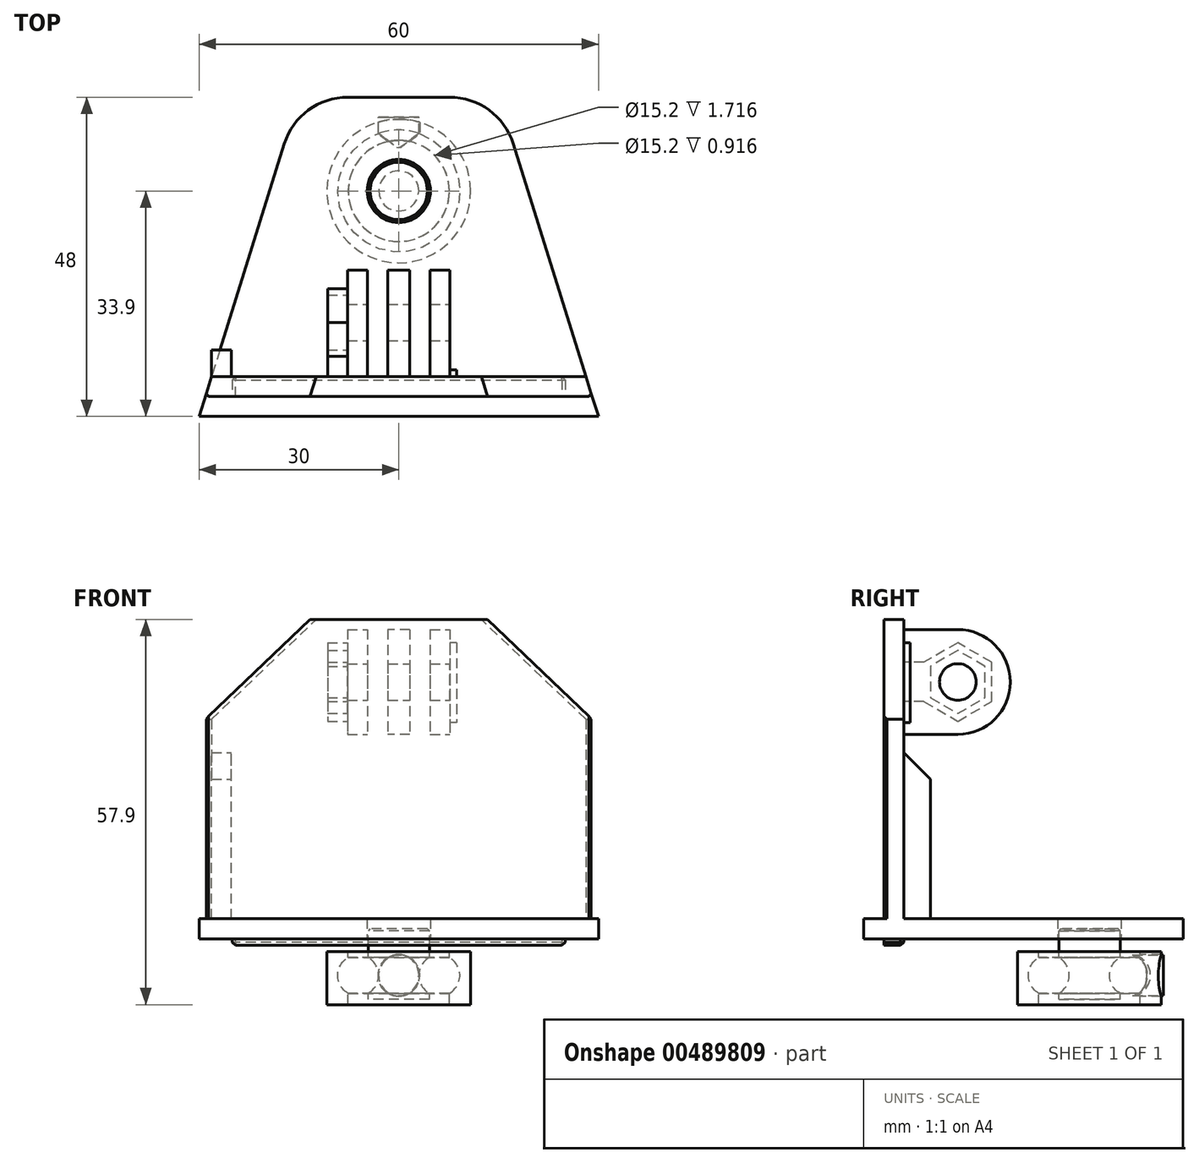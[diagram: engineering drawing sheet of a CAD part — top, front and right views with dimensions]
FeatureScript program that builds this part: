
annotation { "Feature Type Name" : "Feature", "Feature Type Description" : "" }
export const myFeature = defineFeature(function(context is Context, id is Id, definition is map)
    precondition{}
    {
        {
            var Q0;
            Q0=qCreatedBy(makeId("Top.planeOp"),FACE);
            var sketch = newSketch(context, id + "F0", { "sketchPlane" : qUnion([Q0])});
            skArc(sketch, "E0", {"start": v(3, 0) * mm, "mid": v(0, 3) * mm, "end": v(-3, 0) * mm});
            skLineSegment(sketch, "E1", {"start": v(3, 0) * mm, "end": v(-3, 0) * mm});
            skLineSegment(sketch, "E2", {"start": v(0, 0) * mm, "end": v(0, -6.1) * mm, "construction": true});
            skSolve(sketch);
        }
        {
            var Q0;
            Q0=qCreatedBy(makeId("Right.planeOp"),FACE);
            var sketch = newSketch(context, id + "F1", { "sketchPlane" : qUnion([Q0])});
            skCircle(sketch, "E3", {"center": v(0, 0) * mm, "radius": 3.08 * mm});
            skLineSegment(sketch, "E4", {"start": v(0, 0) * mm, "end": v(-12.4, 0) * mm, "construction": true});
            skLineSegment(sketch, "E5", {"start": v(-12.4, 8.14) * mm, "end": v(-12.4, -5.03) * mm, "construction": true});
            skLineSegment(sketch, "E6", {"start": v(0, 0) * mm, "end": v(0, 3.76) * mm, "construction": true});
            skLineSegment(sketch, "E7", {"start": v(-6.1, 3.76) * mm, "end": v(-6.1, -2.41) * mm, "construction": true});
            skSolve(sketch);
        }
        {
            var Q0;
            Q0=sQuery(id+"F1.wireOp",EDGE,"E3");
            var Q1;
            Q1=sQuery(id+"F1.wireOp",EDGE,"E7");
            revolve(context, id + "F2", {"bodyType" : ExtendedToolBodyType.SURFACE, "surfaceEntities" : qUnion([Q0]), "axis" : qUnion([Q1]), "revolveType" : RevolveType.FULL});
        }
        {
            var Q0;
            Q0=qCreatedBy(makeId("Right.planeOp"),FACE);
            var sketch = newSketch(context, id + "F3", { "sketchPlane" : qUnion([Q0])});
            skCircle(sketch, "E8.0", {"center": v(0, 0) * mm, "radius": 3.08 * mm});
            skLineSegment(sketch, "E9.0", {"start": v(-6.1, 3.76) * mm, "end": v(-6.1, -2.41) * mm});
            skLineSegment(sketch, "E9.1", {"start": v(0, 0) * mm, "end": v(-12.4, 0) * mm});
            skPoint(sketch, "E10.rect.middle", {"position": v(-6.1, 0) * mm});
            skLineSegment(sketch, "E11", {"start": v(-1.5, 7) * mm, "end": v(-1.5, -3.6) * mm});
            skLineSegment(sketch, "E12", {"start": v(-1.5, -3.6) * mm, "end": v(-6.1, -3.6) * mm});
            skLineSegment(sketch, "E13", {"start": v(-6.1, -3.6) * mm, "end": v(-6.1, 7) * mm});
            skLineSegment(sketch, "E14", {"start": v(-6.1, 7) * mm, "end": v(-1.5, 7) * mm});
            skLineSegment(sketch, "E15", {"start": v(4.7, 3.6) * mm, "end": v(4.7, -4.4) * mm});
            skLineSegment(sketch, "E16", {"start": v(4.7, -4.4) * mm, "end": v(1.5, -4.4) * mm});
            skLineSegment(sketch, "E17", {"start": v(4.7, 3.6) * mm, "end": v(1.5, 3.6) * mm});
            skLineSegment(sketch, "E18", {"start": v(1.5, 3.6) * mm, "end": v(1.5, -4.4) * mm});
            skSolve(sketch);
        }
        {
            var Q0;
            {var subQ0=sQuery(id+"F3.wireOp",EDGE,"E14");Q0=makeQuery(id+"F3.imprint","IMPRINT",FACE,{"disambiguationData":[TD([[makeQuery(id+"F3.imprint","IMPRINT",EDGE,{"derivedFrom":subQ0}),-1.0]])]});}
            var Q1;
            {var subQ3=sQuery(id+"F3.wireOp",EDGE,"E12");Q1=makeQuery(id+"F3.imprint","IMPRINT",FACE,{"disambiguationData":[TD([[makeQuery(id+"F3.imprint","IMPRINT",EDGE,{"derivedFrom":subQ3}),-1.0]])]});}
            var Q2;
            Q2=sQuery(id+"F3.wireOp",EDGE,"E9.0");
            revolve(context, id + "F4", {"entities" : qUnion([Q0, Q1]), "axis" : qUnion([Q2]), "revolveType" : RevolveType.FULL});
        }
        {
            var Q0;
            Q0=makeQuery(id+"F3.imprint","IMPRINT",FACE,{"disambiguationData":[TD([[makeQuery(id+"F3.imprint","IMPRINT",EDGE,{"derivedFrom":sQuery(id+"F3.wireOp",EDGE,"E15")}),-1.0]])]});
            var Q1;
            Q1=sQuery(id+"F3.wireOp",EDGE,"E9.0");
            revolve(context, id + "F5", {"entities" : qUnion([Q0]), "axis" : qUnion([Q1]), "revolveType" : RevolveType.FULL});
        }
        {
            var Q0;
            Q0=qCreatedBy(makeId("Front.planeOp"),FACE);
            var sketch = newSketch(context, id + "F6", { "sketchPlane" : qUnion([Q0])});
            skCircle(sketch, "E19", {"center": v(0, 0) * mm, "radius": 3.15 * mm});
            skSolve(sketch);
        }
        {
            var Q0;
            Q0=makeQuery(id+"F6.imprint","IMPRINT",FACE,{"disambiguationData":[TD([[makeQuery(id+"F6.imprint","IMPRINT",EDGE,{"derivedFrom":sQuery(id+"F6.wireOp",EDGE,"E19")}),1.0]])]});
            var Q1;
            Q1=makeQuery(id+"F5.opRevolve","SWEPT_FACE",FACE,{"disambiguationData":[OSD([sQuery(id+"F3.wireOp",EDGE,"E15")])]});
            extrude(context, id + "F7", {"entities" : qUnion([Q0]), "operationType" : NewBodyOperationType.REMOVE, "endBound" : BoundingType.UP_TO_SURFACE, "oppositeDirection" : true, "endBoundEntityFace" : qUnion([Q1]), "depth" : 25 * mm});
        }
        {
            var Q0;
            Q0=qCreatedBy(makeId("Front.planeOp"),FACE);
            var sketch = newSketch(context, id + "F8", { "sketchPlane" : qUnion([Q0])});
            skLineSegment(sketch, "E20.rect.bottom", {"start": v(13.05, 1.97) * mm, "end": v(8.99, 1.97) * mm});
            skLineSegment(sketch, "E20.rect.top", {"start": v(13.05, 8.89) * mm, "end": v(8.99, 8.89) * mm});
            skLineSegment(sketch, "E20.rect.left", {"start": v(13.05, 1.97) * mm, "end": v(13.05, 8.89) * mm});
            skLineSegment(sketch, "E20.rect.right", {"start": v(8.99, 1.97) * mm, "end": v(8.99, 8.89) * mm});
            skPoint(sketch, "E20.rect.middle", {"position": v(11.02, 5.43) * mm});
            skSolve(sketch);
        }
        {
            var Q0;
            Q0=makeQuery(id+"F8.imprint","IMPRINT",FACE,{"disambiguationData":[TD([[makeQuery(id+"F8.imprint","IMPRINT",EDGE,{"derivedFrom":sQuery(id+"F8.wireOp",EDGE,"E20.rect.bottom")}),-1.0]])]});
            cPlane(context, id + "F9", {"entities" : qUnion([Q0]), "cplaneType" : CPlaneType.OFFSET, "offset" : 5 * mm, "oppositeDirection" : true, "width" : 150 * mm, "height" : 150 * mm});
        }
        {
            var Q0;
            Q0=qCreatedBy(id+"F9.planeOp",FACE);
            var sketch = newSketch(context, id + "F10", { "sketchPlane" : qUnion([Q0])});
            skCircle(sketch, "E21", {"center": v(0, 0) * mm, "radius": 3.05 * mm});
            skSolve(sketch);
        }
        {
            var Q0;
            Q0=makeQuery(id+"F10.imprint","IMPRINT",FACE,{"disambiguationData":[TD([[makeQuery(id+"F10.imprint","IMPRINT",EDGE,{"derivedFrom":sQuery(id+"F10.wireOp",EDGE,"E21")}),1.0]])]});
            var Q1;
            Q1=makeQuery(id+"F5.opRevolve","SWEPT_FACE",FACE,{"disambiguationData":[OSD([sQuery(id+"F3.wireOp",EDGE,"E8.0")])]});
            extrude(context, id + "F11", {"entities" : qUnion([Q0]), "endBound" : BoundingType.UP_TO_SURFACE, "endBoundEntityFace" : qUnion([Q1]), "depth" : 25 * mm});
        }
        {
            var Q0;
            Q0=makeQuery(id+"F4.opRevolve","SWEPT_EDGE",EDGE,{"disambiguationData":[OSD([sQuery(id+"F3.wireOp",EDGE,"E11"),sQuery(id+"F3.wireOp",EDGE,"E14")])]});
            chamfer(context, id + "F12", {"entities" : qUnion([Q0]), "width" : 0.3 * mm, "tangentPropagation" : true});
        }
        {
            var Q0;
            Q0=makeQuery(id+"F4.opRevolve","SWEPT_FACE",FACE,{"disambiguationData":[OSD([sQuery(id+"F3.wireOp",EDGE,"E14")])]});
            var sketch = newSketch(context, id + "F13", { "sketchPlane" : qUnion([Q0])});
            skLineSegment(sketch, "E22.bottom", {"start": v(-25, -34) * mm, "end": v(25, -34) * mm});
            skLineSegment(sketch, "E22.top", {"start": v(-25, -37) * mm, "end": v(25, -37) * mm});
            skLineSegment(sketch, "E22.left", {"start": v(-25, -34) * mm, "end": v(-25, -37) * mm});
            skLineSegment(sketch, "E22.right", {"start": v(25, -34) * mm, "end": v(25, -37) * mm});
            skLineSegment(sketch, "E23", {"start": v(-30, -40) * mm, "end": v(30, -40) * mm});
            skLineSegment(sketch, "E24", {"start": v(-15, 8) * mm, "end": v(15, 8) * mm});
            skLineSegment(sketch, "E25", {"start": v(-15, 8) * mm, "end": v(-30, -40) * mm});
            skLineSegment(sketch, "E26", {"start": v(15, 8) * mm, "end": v(30, -40) * mm});
            skCircle(sketch, "E27.0", {"center": v(0, -6.1) * mm, "radius": 4.75 * mm});
            skSolve(sketch);
        }
        {
            var Q0;
            Q0=makeQuery(id+"F13.imprint","IMPRINT",FACE,{"disambiguationData":[TD([[makeQuery(id+"F13.imprint","IMPRINT",EDGE,{"derivedFrom":sQuery(id+"F13.wireOp",EDGE,"E22.bottom")}),1.0]])]});
            extrude(context, id + "F14", {"entities" : qUnion([Q0]), "depth" : 3 * mm, "symmetric" : true});
        }
        {
            var Q0;
            Q0=makeQuery(id+"F14.opExtrude","SWEPT_EDGE",EDGE,{"disambiguationData":[OSD([sQuery(id+"F13.wireOp",EDGE,"E24"),sQuery(id+"F13.wireOp",EDGE,"E25")])]});
            var Q1;
            Q1=makeQuery(id+"F14.opExtrude","SWEPT_EDGE",EDGE,{"disambiguationData":[OSD([sQuery(id+"F13.wireOp",EDGE,"E24"),sQuery(id+"F13.wireOp",EDGE,"E26")])]});
            fillet(context, id + "F15", {"entities" : qUnion([Q0, Q1]), "radius" : 10 * mm, "tangentPropagation" : true, "allowEdgeOverflow" : false});
        }
        {
            var Q0;
            Q0=makeQuery(id+"F14.opExtrude","CAP_FACE",FACE,{"disambiguationData":[OSD([sQuery(id+"F13.wireOp",EDGE,"E22.bottom"),sQuery(id+"F13.wireOp",EDGE,"E22.top"),sQuery(id+"F13.wireOp",EDGE,"E22.left"),sQuery(id+"F13.wireOp",EDGE,"E22.right"),sQuery(id+"F13.wireOp",EDGE,"E23"),sQuery(id+"F13.wireOp",EDGE,"E24"),sQuery(id+"F13.wireOp",EDGE,"E25"),sQuery(id+"F13.wireOp",EDGE,"E26"),sQuery(id+"F13.wireOp",EDGE,"E27.0")])],"isStart":false});
            var sketch = newSketch(context, id + "F16", { "sketchPlane" : qUnion([Q0])});
            skLineSegment(sketch, "E28.0", {"start": v(-25, -37) * mm, "end": v(25, -37) * mm});
            skLineSegment(sketch, "E28.1", {"start": v(-25, -34) * mm, "end": v(-25, -37) * mm});
            skLineSegment(sketch, "E28.2", {"start": v(-25, -34) * mm, "end": v(25, -34) * mm});
            skLineSegment(sketch, "E28.3", {"start": v(25, -34) * mm, "end": v(25, -37) * mm});
            skLineSegment(sketch, "E29", {"start": v(-25, -34) * mm, "end": v(-28.12, -34) * mm});
            skLineSegment(sketch, "E30", {"start": v(-28.12, -34) * mm, "end": v(-29.06, -37) * mm});
            skLineSegment(sketch, "E31", {"start": v(-29.06, -37) * mm, "end": v(-25, -37) * mm});
            skLineSegment(sketch, "E32", {"start": v(25, -34) * mm, "end": v(28.12, -34) * mm});
            skLineSegment(sketch, "E33", {"start": v(28.12, -34) * mm, "end": v(29.06, -37) * mm});
            skLineSegment(sketch, "E34", {"start": v(29.06, -37) * mm, "end": v(25, -37) * mm});
            skSolve(sketch);
        }
        {
            var Q0;
            Q0=makeQuery(id+"F16.imprint","IMPRINT",FACE,{"disambiguationData":[TD([[makeQuery(id+"F16.imprint","IMPRINT",EDGE,{"derivedFrom":sQuery(id+"F16.wireOp",EDGE,"E28.3")}),1.0]])]});
            var Q1;
            Q1=makeQuery(id+"F16.imprint","IMPRINT",FACE,{"disambiguationData":[TD([[makeQuery(id+"F16.imprint","IMPRINT",EDGE,{"derivedFrom":sQuery(id+"F16.wireOp",EDGE,"E28.1")}),-1.0]])]});
            var Q2;
            Q2=makeQuery(id+"F16.imprint","IMPRINT",FACE,{"disambiguationData":[TD([[makeQuery(id+"F16.imprint","IMPRINT",EDGE,{"derivedFrom":sQuery(id+"F16.wireOp",EDGE,"E28.0")}),1.0]])]});
            extrude(context, id + "F17", {"entities" : qUnion([Q0, Q1, Q2]), "depth" : 45 * mm});
        }
        {
            var Q0;
            Q0=makeQuery(id+"F16.imprint","IMPRINT",FACE,{"disambiguationData":[TD([[makeQuery(id+"F16.imprint","IMPRINT",EDGE,{"derivedFrom":sQuery(id+"F16.wireOp",EDGE,"E28.0")}),1.0]])]});
            var Q1;
            Q1=makeQuery(id+"F14.opExtrude","CAP_FACE",FACE,{"disambiguationData":[OSD([sQuery(id+"F13.wireOp",EDGE,"E22.bottom"),sQuery(id+"F13.wireOp",EDGE,"E22.top"),sQuery(id+"F13.wireOp",EDGE,"E22.left"),sQuery(id+"F13.wireOp",EDGE,"E22.right"),sQuery(id+"F13.wireOp",EDGE,"E23"),sQuery(id+"F13.wireOp",EDGE,"E24"),sQuery(id+"F13.wireOp",EDGE,"E25"),sQuery(id+"F13.wireOp",EDGE,"E26"),sQuery(id+"F13.wireOp",EDGE,"E27.0")])],"isStart":true});
            extrude(context, id + "F18", {"entities" : qUnion([Q0]), "operationType" : NewBodyOperationType.ADD, "oppositeDirection" : true, "endBoundEntity" : qUnion([Q1]), "depth" : 4 * mm});
        }
        {
            var Q0;
            Q0=makeQuery(id+"F18.opExtrude","SWEPT_EDGE",EDGE,{"disambiguationData":[OSD([sQuery(id+"F16.wireOp",EDGE,"E28.2"),sQuery(id+"F16.wireOp",EDGE,"E28.3"),sQuery(id+"F16.wireOp",EDGE,"E32")])]});
            var Q1;
            Q1=makeQuery(id+"F18.opExtrude","SWEPT_EDGE",EDGE,{"disambiguationData":[OSD([sQuery(id+"F16.wireOp",EDGE,"E28.1"),sQuery(id+"F16.wireOp",EDGE,"E28.2"),sQuery(id+"F16.wireOp",EDGE,"E29")])]});
            var Q2;
            Q2=makeQuery(id+"F18.opExtrude","CAP_EDGE",EDGE,{"disambiguationData":[OSD([sQuery(id+"F16.wireOp",EDGE,"E28.2")])],"isStart":false});
            var Q3;
            Q3=makeQuery(id+"F18.opExtrude","CAP_EDGE",EDGE,{"disambiguationData":[OSD([sQuery(id+"F16.wireOp",EDGE,"E28.3")])],"isStart":false});
            var Q4;
            Q4=makeQuery(id+"F18.opExtrude","CAP_EDGE",EDGE,{"disambiguationData":[OSD([sQuery(id+"F16.wireOp",EDGE,"E28.1")])],"isStart":false});
            chamfer(context, id + "F19", {"entities" : qUnion([Q0, Q1, Q2, Q3, Q4]), "width" : 0.5 * mm, "tangentPropagation" : true});
        }
        {
            var Q0;
            Q0=makeQuery(id+"F17.opExtrude","SWEPT_EDGE",EDGE,{"disambiguationData":[OSD([sQuery(id+"F13.wireOp",EDGE,"E26"),sQuery(id+"F16.wireOp",EDGE,"E33"),sQuery(id+"F16.wireOp",EDGE,"E34")])]});
            var Q1;
            Q1=makeQuery(id+"F17.opExtrude","SWEPT_EDGE",EDGE,{"disambiguationData":[OSD([sQuery(id+"F13.wireOp",EDGE,"E25"),sQuery(id+"F16.wireOp",EDGE,"E30"),sQuery(id+"F16.wireOp",EDGE,"E31")])]});
            chamfer(context, id + "F20", {"entities" : qUnion([Q0, Q1]), "width" : 0.5 * mm, "tangentPropagation" : true});
        }
        {
            var Q0;
            {var subQ0=sQuery(id+"F16.wireOp",EDGE,"E28.2");Q0=makeQuery(id+"F18.boolean.opBoolean","MERGE",FACE,{"derivedFrom":[makeQuery(id+"F17.opExtrude","SWEPT_FACE",FACE,{"disambiguationData":[OSD([subQ0,sQuery(id+"F16.wireOp",EDGE,"E29"),sQuery(id+"F16.wireOp",EDGE,"E32")])]}),makeQuery(id+"F18.opExtrude","SWEPT_FACE",FACE,{"disambiguationData":[OSD([subQ0])]})]});}
            var sketch = newSketch(context, id + "F21", { "sketchPlane" : qUnion([Q0])});
            skLineSegment(sketch, "E35.rect.bottom", {"start": v(-1.65, 51.98) * mm, "end": v(1.65, 51.98) * mm});
            skLineSegment(sketch, "E35.rect.top", {"start": v(-1.65, 36.23) * mm, "end": v(1.65, 36.23) * mm});
            skLineSegment(sketch, "E35.rect.left", {"start": v(-1.65, 51.98) * mm, "end": v(-1.65, 36.23) * mm});
            skLineSegment(sketch, "E35.rect.right", {"start": v(1.65, 51.98) * mm, "end": v(1.65, 36.23) * mm});
            skPoint(sketch, "E35.rect.middle", {"position": v(0, 44.1) * mm});
            skLineSegment(sketch, "E36.bottom", {"start": v(-4.7, 51.98) * mm, "end": v(-7.7, 51.98) * mm});
            skLineSegment(sketch, "E36.top", {"start": v(-4.7, 36.23) * mm, "end": v(-7.7, 36.23) * mm});
            skLineSegment(sketch, "E36.left", {"start": v(-4.7, 51.98) * mm, "end": v(-4.7, 36.23) * mm});
            skLineSegment(sketch, "E36.right", {"start": v(-7.7, 51.98) * mm, "end": v(-7.7, 36.23) * mm});
            skLineSegment(sketch, "E37.bottom", {"start": v(7.7, 51.98) * mm, "end": v(4.7, 51.98) * mm});
            skLineSegment(sketch, "E37.top", {"start": v(7.7, 36.23) * mm, "end": v(4.7, 36.23) * mm});
            skLineSegment(sketch, "E37.left", {"start": v(7.7, 51.98) * mm, "end": v(7.7, 36.23) * mm});
            skLineSegment(sketch, "E37.right", {"start": v(4.7, 51.98) * mm, "end": v(4.7, 36.23) * mm});
            skSolve(sketch);
        }
        {
            var Q0;
            Q0=makeQuery(id+"F21.imprint","IMPRINT",FACE,{"disambiguationData":[TD([[makeQuery(id+"F21.imprint","IMPRINT",EDGE,{"derivedFrom":sQuery(id+"F21.wireOp",EDGE,"E36.bottom")}),1.0]])]});
            var Q1;
            Q1=makeQuery(id+"F21.imprint","IMPRINT",FACE,{"disambiguationData":[TD([[makeQuery(id+"F21.imprint","IMPRINT",EDGE,{"derivedFrom":sQuery(id+"F21.wireOp",EDGE,"E35.rect.bottom")}),-1.0]])]});
            var Q2;
            Q2=makeQuery(id+"F21.imprint","IMPRINT",FACE,{"disambiguationData":[TD([[makeQuery(id+"F21.imprint","IMPRINT",EDGE,{"derivedFrom":sQuery(id+"F21.wireOp",EDGE,"E37.bottom")}),1.0]])]});
            extrude(context, id + "F22", {"entities" : qUnion([Q0, Q1, Q2]), "operationType" : NewBodyOperationType.ADD, "depth" : 16 * mm});
        }
        {
            var Q0;
            {var subQ0=sQuery(id+"F16.wireOp",EDGE,"E28.2");Q0=makeQuery(id+"F18.boolean.opBoolean","MERGE",FACE,{"derivedFrom":[makeQuery(id+"F17.opExtrude","SWEPT_FACE",FACE,{"disambiguationData":[OSD([subQ0,sQuery(id+"F16.wireOp",EDGE,"E29"),sQuery(id+"F16.wireOp",EDGE,"E32")])]}),makeQuery(id+"F18.opExtrude","SWEPT_FACE",FACE,{"disambiguationData":[OSD([subQ0])]})]});}
            var sketch = newSketch(context, id + "F23", { "sketchPlane" : qUnion([Q0])});
            skLineSegment(sketch, "E38.bottom", {"start": v(-28.12, 8.5) * mm, "end": v(-25.12, 8.5) * mm});
            skLineSegment(sketch, "E38.top", {"start": v(-28.13, 33.5) * mm, "end": v(-25.12, 33.5) * mm});
            skLineSegment(sketch, "E38.left", {"start": v(-28.12, 8.5) * mm, "end": v(-28.13, 33.5) * mm});
            skLineSegment(sketch, "E38.right", {"start": v(-25.12, 8.5) * mm, "end": v(-25.12, 33.5) * mm});
            skLineSegment(sketch, "E39.bottom", {"start": v(28.12, 8.5) * mm, "end": v(25.12, 8.5) * mm});
            skLineSegment(sketch, "E39.top", {"start": v(28.12, 33.5) * mm, "end": v(25.12, 33.5) * mm});
            skLineSegment(sketch, "E39.left", {"start": v(28.12, 8.5) * mm, "end": v(28.12, 33.5) * mm});
            skLineSegment(sketch, "E39.right", {"start": v(25.12, 8.5) * mm, "end": v(25.12, 33.5) * mm});
            skSolve(sketch);
        }
        {
            var Q0;
            {Q0=qUnion([makeQuery(id+"F23.imprint","IMPRINT",FACE,{"disambiguationData":[TD([[makeQuery(id+"F23.imprint","IMPRINT",EDGE,{"derivedFrom":sQuery(id+"F23.wireOp",EDGE,"E38.bottom")}),-1.0]])]}),makeQuery(id+"F23.imprint","IMPRINT",FACE,{"disambiguationData":[TD([[makeQuery(id+"F23.imprint","IMPRINT",EDGE,{"derivedFrom":sQuery(id+"F23.wireOp",EDGE,"E39.bottom")}),-1.0]])]})]);}
            extrude(context, id + "F24", {"entities" : qUnion([Q0]), "operationType" : NewBodyOperationType.ADD, "depth" : 4 * mm});
        }
        {
            var Q0;
            Q0=makeQuery(id+"F24.opExtrude","CAP_EDGE",EDGE,{"disambiguationData":[OSD([sQuery(id+"F23.wireOp",EDGE,"E38.top")])],"isStart":false});
            var Q1;
            Q1=makeQuery(id+"F24.opExtrude","CAP_EDGE",EDGE,{"disambiguationData":[OSD([sQuery(id+"F23.wireOp",EDGE,"E39.top")])],"isStart":false});
            chamfer(context, id + "F25", {"entities" : qUnion([Q0, Q1]), "width" : 4 * mm, "tangentPropagation" : true});
        }
        {
            var Q0;
            Q0=makeQuery(id+"F22.opExtrude","SWEPT_FACE",FACE,{"disambiguationData":[OSD([sQuery(id+"F21.wireOp",EDGE,"E36.right")])]});
            var sketch = newSketch(context, id + "F26", { "sketchPlane" : qUnion([Q0])});
            skCircle(sketch, "E40", {"center": v(-25.88, 44.1) * mm, "radius": 2.75 * mm});
            skSolve(sketch);
        }
        {
            var Q0;
            Q0=makeQuery(id+"F26.imprint","IMPRINT",FACE,{"disambiguationData":[TD([[makeQuery(id+"F26.imprint","IMPRINT",EDGE,{"derivedFrom":sQuery(id+"F26.wireOp",EDGE,"E40")}),1.0]])]});
            extrude(context, id + "F27", {"entities" : qUnion([Q0]), "operationType" : NewBodyOperationType.REMOVE, "oppositeDirection" : true, "depth" : 25 * mm});
        }
        {
            var Q0;
            Q0=makeQuery(id+"F22.opExtrude","CAP_EDGE",EDGE,{"disambiguationData":[OSD([sQuery(id+"F21.wireOp",EDGE,"E36.bottom")])],"isStart":false});
            var Q1;
            Q1=makeQuery(id+"F22.opExtrude","CAP_EDGE",EDGE,{"disambiguationData":[OSD([sQuery(id+"F21.wireOp",EDGE,"E35.rect.bottom")])],"isStart":false});
            var Q2;
            Q2=makeQuery(id+"F22.opExtrude","CAP_EDGE",EDGE,{"disambiguationData":[OSD([sQuery(id+"F21.wireOp",EDGE,"E37.bottom")])],"isStart":false});
            var Q3;
            Q3=makeQuery(id+"F22.opExtrude","CAP_EDGE",EDGE,{"disambiguationData":[OSD([sQuery(id+"F21.wireOp",EDGE,"E37.top")])],"isStart":false});
            var Q4;
            Q4=makeQuery(id+"F22.opExtrude","CAP_EDGE",EDGE,{"disambiguationData":[OSD([sQuery(id+"F21.wireOp",EDGE,"E35.rect.top")])],"isStart":false});
            var Q5;
            Q5=makeQuery(id+"F22.opExtrude","CAP_EDGE",EDGE,{"disambiguationData":[OSD([sQuery(id+"F21.wireOp",EDGE,"E36.top")])],"isStart":false});
            fillet(context, id + "F28", {"entities" : qUnion([Q0, Q1, Q2, Q3, Q4, Q5]), "radius" : 7.88 * mm, "tangentPropagation" : true, "allowEdgeOverflow" : false});
        }
        {
            var Q0;
            Q0=makeQuery(id+"F17.opExtrude","CAP_EDGE",EDGE,{"disambiguationData":[OSD([sQuery(id+"F16.wireOp",EDGE,"E30")])],"isStart":false});
            var Q1;
            Q1=makeQuery(id+"F17.opExtrude","CAP_EDGE",EDGE,{"disambiguationData":[OSD([sQuery(id+"F16.wireOp",EDGE,"E33")])],"isStart":false});
            chamfer(context, id + "F29", {"entities" : qUnion([Q0, Q1]), "width" : 15 * mm, "tangentPropagation" : true});
        }
        {
            var Q0;
            Q0=makeQuery(id+"F22.opExtrude","SWEPT_FACE",FACE,{"disambiguationData":[OSD([sQuery(id+"F21.wireOp",EDGE,"E37.left")])]});
            var sketch = newSketch(context, id + "F30", { "sketchPlane" : qUnion([Q0])});
            skCircle(sketch, "E41.0", {"center": v(25.88, 44.1) * mm, "radius": 2.75 * mm});
            skCircle(sketch, "E42.cCircle", {"center": v(25.88, 44.1) * mm, "radius": 4.1 * mm, "construction": true});
            skLineSegment(sketch, "E42.0", {"start": v(29.98, 46.47) * mm, "end": v(29.98, 41.73) * mm});
            skLineSegment(sketch, "E42.1", {"start": v(29.97, 41.73) * mm, "end": v(25.88, 39.37) * mm});
            skLineSegment(sketch, "E42.2", {"start": v(25.88, 39.37) * mm, "end": v(21.78, 41.73) * mm});
            skLineSegment(sketch, "E42.3", {"start": v(21.78, 41.73) * mm, "end": v(21.78, 46.47) * mm});
            skLineSegment(sketch, "E42.4", {"start": v(21.78, 46.47) * mm, "end": v(25.88, 48.83) * mm});
            skLineSegment(sketch, "E42.5", {"start": v(25.88, 48.83) * mm, "end": v(29.98, 46.47) * mm});
            skPoint(sketch, "E42.0.midPoint", {"position": v(29.98, 44.1) * mm});
            skLineSegment(sketch, "E43.0", {"start": v(20.78, 47.04) * mm, "end": v(25.88, 49.99) * mm});
            skLineSegment(sketch, "E43.1", {"start": v(20.78, 41.16) * mm, "end": v(20.78, 47.04) * mm});
            skLineSegment(sketch, "E43.2", {"start": v(25.88, 38.21) * mm, "end": v(20.78, 41.16) * mm});
            skLineSegment(sketch, "E43.3", {"start": v(30.98, 41.16) * mm, "end": v(25.88, 38.21) * mm});
            skLineSegment(sketch, "E43.4", {"start": v(30.97, 47.04) * mm, "end": v(30.97, 41.16) * mm});
            skLineSegment(sketch, "E43.5", {"start": v(25.88, 49.99) * mm, "end": v(30.97, 47.04) * mm});
            skLineSegment(sketch, "E44.bottom", {"start": v(30.98, 41.16) * mm, "end": v(34, 41.16) * mm});
            skLineSegment(sketch, "E44.top", {"start": v(30.98, 47.04) * mm, "end": v(34, 47.04) * mm});
            skLineSegment(sketch, "E44.left", {"start": v(30.98, 41.16) * mm, "end": v(30.98, 47.04) * mm});
            skLineSegment(sketch, "E44.right", {"start": v(34, 41.16) * mm, "end": v(34, 47.04) * mm});
            skSolve(sketch);
        }
        {
            var Q0;
            Q0=makeQuery(id+"F30.imprint","IMPRINT",FACE,{"disambiguationData":[TD([[makeQuery(id+"F30.imprint","IMPRINT",EDGE,{"derivedFrom":sQuery(id+"F30.wireOp",EDGE,"E42.0")}),1.0]])]});
            var Q1;
            Q1=makeQuery(id+"F30.imprint","IMPRINT",FACE,{"disambiguationData":[TD([[makeQuery(id+"F30.imprint","IMPRINT",EDGE,{"derivedFrom":sQuery(id+"F30.wireOp",EDGE,"E44.bottom")}),1.0]])]});
            extrude(context, id + "F31", {"entities" : qUnion([Q0, Q1]), "operationType" : NewBodyOperationType.ADD, "depth" : 3 * mm});
        }
        {
            var Q0;
            Q0=makeQuery(id+"F22.opExtrude","SWEPT_FACE",FACE,{"disambiguationData":[OSD([sQuery(id+"F21.wireOp",EDGE,"E36.right")])]});
            var sketch = newSketch(context, id + "F32", { "sketchPlane" : qUnion([Q0])});
            skLineSegment(sketch, "E45.bottom", {"start": v(-33, 49.98) * mm, "end": v(-34, 49.98) * mm});
            skLineSegment(sketch, "E45.top", {"start": v(-33, 37.97) * mm, "end": v(-34, 37.97) * mm});
            skLineSegment(sketch, "E45.left", {"start": v(-33, 49.98) * mm, "end": v(-33, 37.97) * mm});
            skLineSegment(sketch, "E45.right", {"start": v(-34, 49.97) * mm, "end": v(-34, 37.97) * mm});
            skSolve(sketch);
        }
        {
            var Q0;
            Q0=makeQuery(id+"F32.imprint","IMPRINT",FACE,{"disambiguationData":[TD([[makeQuery(id+"F32.imprint","IMPRINT",EDGE,{"derivedFrom":sQuery(id+"F32.wireOp",EDGE,"E45.bottom")}),1.0]])]});
            extrude(context, id + "F33", {"entities" : qUnion([Q0]), "operationType" : NewBodyOperationType.ADD, "depth" : 1 * mm});
        }
    });
